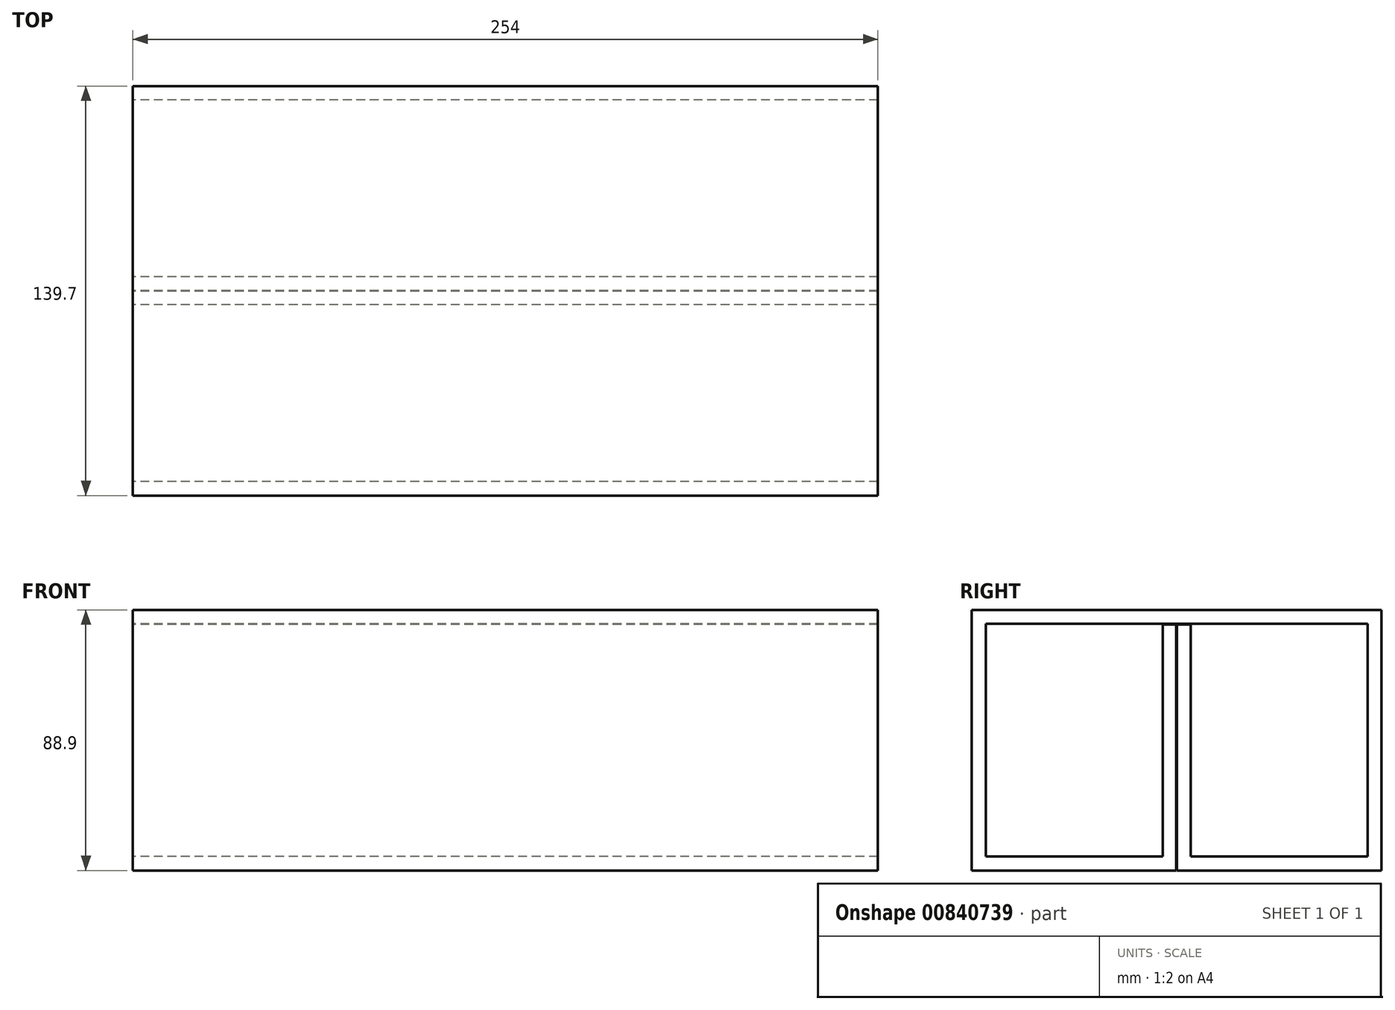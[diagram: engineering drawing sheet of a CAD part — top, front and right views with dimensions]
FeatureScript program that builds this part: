
annotation { "Feature Type Name" : "Feature", "Feature Type Description" : "" }
export const myFeature = defineFeature(function(context is Context, id is Id, definition is map)
    precondition{}
    {
        {
            var Q0;
            Q0=qCreatedBy(makeId("Right.planeOp"),FACE);
            var sketch = newSketch(context, id + "F0", { "sketchPlane" : qUnion([Q0])});
            skLineSegment(sketch, "E0", {"start": v(0, 0) * mm, "end": v(0, 126.35) * mm, "construction": true});
            skLineSegment(sketch, "E1.bottom", {"start": v(-69.85, 88.9) * mm, "end": v(69.85, 88.9) * mm});
            skLineSegment(sketch, "E1.top", {"start": v(-69.85, 0) * mm, "end": v(-0.13, 0) * mm});
            skLineSegment(sketch, "E1.left", {"start": v(-69.85, 88.9) * mm, "end": v(-69.85, 0) * mm});
            skLineSegment(sketch, "E2.0", {"start": v(-65.09, 84.14) * mm, "end": v(65.09, 84.14) * mm});
            skLineSegment(sketch, "E2.1", {"start": v(-65.09, 84.14) * mm, "end": v(-65.09, 4.76) * mm});
            skLineSegment(sketch, "E2.2", {"start": v(-65.09, 4.76) * mm, "end": v(-4.76, 4.76) * mm});
            skLineSegment(sketch, "E2.3", {"start": v(-4.76, 83.88) * mm, "end": v(-4.76, 4.76) * mm});
            skLineSegment(sketch, "E3.MirrorCS", {"start": v(69.85, 88.9) * mm, "end": v(69.85, 0) * mm});
            skLineSegment(sketch, "E4.MirrorCS", {"start": v(4.76, 83.88) * mm, "end": v(4.76, 4.76) * mm});
            skLineSegment(sketch, "E5.MirrorCS", {"start": v(65.09, 4.76) * mm, "end": v(4.76, 4.76) * mm});
            skLineSegment(sketch, "E6.MirrorCS", {"start": v(65.09, 84.14) * mm, "end": v(65.09, 4.76) * mm});
            skLineSegment(sketch, "E7.left", {"start": v(-0.13, 0) * mm, "end": v(-0.13, 83.88) * mm});
            skLineSegment(sketch, "E7.right", {"start": v(0.13, 0) * mm, "end": v(0.13, 83.88) * mm});
            skLineSegment(sketch, "E8.trimOffspring", {"start": v(0.13, 0) * mm, "end": v(69.85, 0) * mm});
            skLineSegment(sketch, "E9", {"start": v(-4.76, 83.88) * mm, "end": v(-0.13, 83.88) * mm});
            skPoint(sketch, "E10.orphan", {"position": v(4.76, 84.14) * mm});
            skLineSegment(sketch, "E11.trimOffspring", {"start": v(0.13, 83.88) * mm, "end": v(4.76, 83.88) * mm});
            skPoint(sketch, "E12.orphan", {"position": v(-4.76, 84.14) * mm});
            skSolve(sketch);
        }
        {
            var Q0;
            Q0=qSketchRegion(id+"F0",true);
            extrude(context, id + "F1", {"entities" : qUnion([Q0]), "endBound" : BoundingType.SYMMETRIC, "depth" : 254 * mm, "offsetDistance" : 25.4 * mm});
        }
    });
